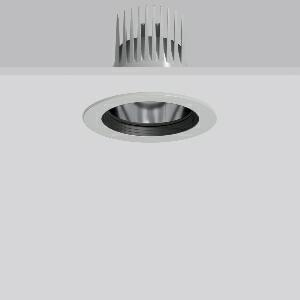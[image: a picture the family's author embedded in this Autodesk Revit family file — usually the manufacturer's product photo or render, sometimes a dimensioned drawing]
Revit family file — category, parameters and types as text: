
# Revit family: heledon_maxi_e_901757_004_3_76_cf1a
name_source: partatom
category: Lighting Fixtures
units: mm (PartAtom-declared; Revit-internal decimal feet)

## family parameters
Cut with Voids When Loaded = No
Host = Face
Light Source = No
Part Type = Normal
Room Calculation Point = No
Round Connector Dimension = Use Diameter
Shared = No

## types (1)
- HELEDON maxi E (1 x LED Modul 935, 3400 lm, 3500)
    Apparent Load = 25 VA
    Approval mark = CE
    CIE Flux Codes = 100 100 100 100 100
    Color Rendering = 92
    Color Temperature = 3500
    Default Elevation = 1800 mm
    Description = Series: HELEDON maxi
Round recessed downlight. Housing: die-cast aluminium, powder-coated. Black plastic ring and recessed LED to prevent glare from the side. Optical assembly with reflector made of MIRO-Silver with 98% total light reflection for outstanding efficiency - can be changed without tools. Best colour rendering index Ra>90. Suitable for Recessed ceiling mounting. Installation without tools thanks to spring fastening system. Including separate LED converter with connecting cable 600 mm.High quality converter without flickering and stroboscopic effect. Through-wiring box (5 pole) available as accessory. The following accessories can be mounted without use of tools: interchangeable lenses, decorative glasses, honeycomb louvre, clear and frosted diffusers, white interchangeable plastic ring. 
Colour: silver
Diameter: 162 mm
Height: 3 mm
Cut-out diameter: 152 mm
Recess height: 200 mm
Luminaire: recess height: 135 mm
Lamp: LED
Socket: without socket
Colour temperature: 3500K
Colour rendering index (CRI): 92
System power: 25 W
Rated luminous flux: 3400 lm
Luminous efficiency: 136 lm/W
Control gear: Converter, dimmable, DALI
Protection class: II
Type of protection: IP 20
    Height = 0 mm  [stored 0 ft]
    Lamp = 1 x LED Modul 935
    Lamp Light Flux = 3400 lm
    Lamp count = 1
    Length = 162 mm
    Lifetime = 50000 h
    Luminous efficacy = 136 lm/W
    Manufacturer = RZB
    ModVariant = No
    Model = 901757.004.3.76
    Mounting Place = Ceiling
    Mounting Type = Recessed
    Number of Poles = 1
    OnlyDefault = Yes
    Power Factor = 1
    Product Name = HELEDON maxi E
    Product group = Recessed downlights
    ProductGroupID = 402
    Protection Class = Protection class II
    Protection Degree = IP 20
    RLX_Detail_Level = 1
    RLX_Emergency_Light_Flux = 0 lm
    RLX_Emergency_Type = 0
    RLX_Emergency_Type_DB = No
    RlxData = <blob elided: 119225 chars, md5=5ac22feb>
    Socket = socket
    Standby Power = 0 W
    System Light Flux = 3400 lm
    System Power = 25 W
    Type Comments = Product without accessories
    Type Image = 901662.004.jpg
    URL = http://relux.com
    VarID = ---
    Voltage = 230 V
    Voltage Range = 220-240 V
    Weight = 0.00 kg
    Width = 0 mm  [stored 0 ft]

note: [stored X ft] marks values corroborated as IEEE doubles in the binary element streams (Revit-internal decimal feet)

## geometry (parser evidence)
native form markers: Blend x4, Sweep x13
no freeform markers — native parametric forms only
